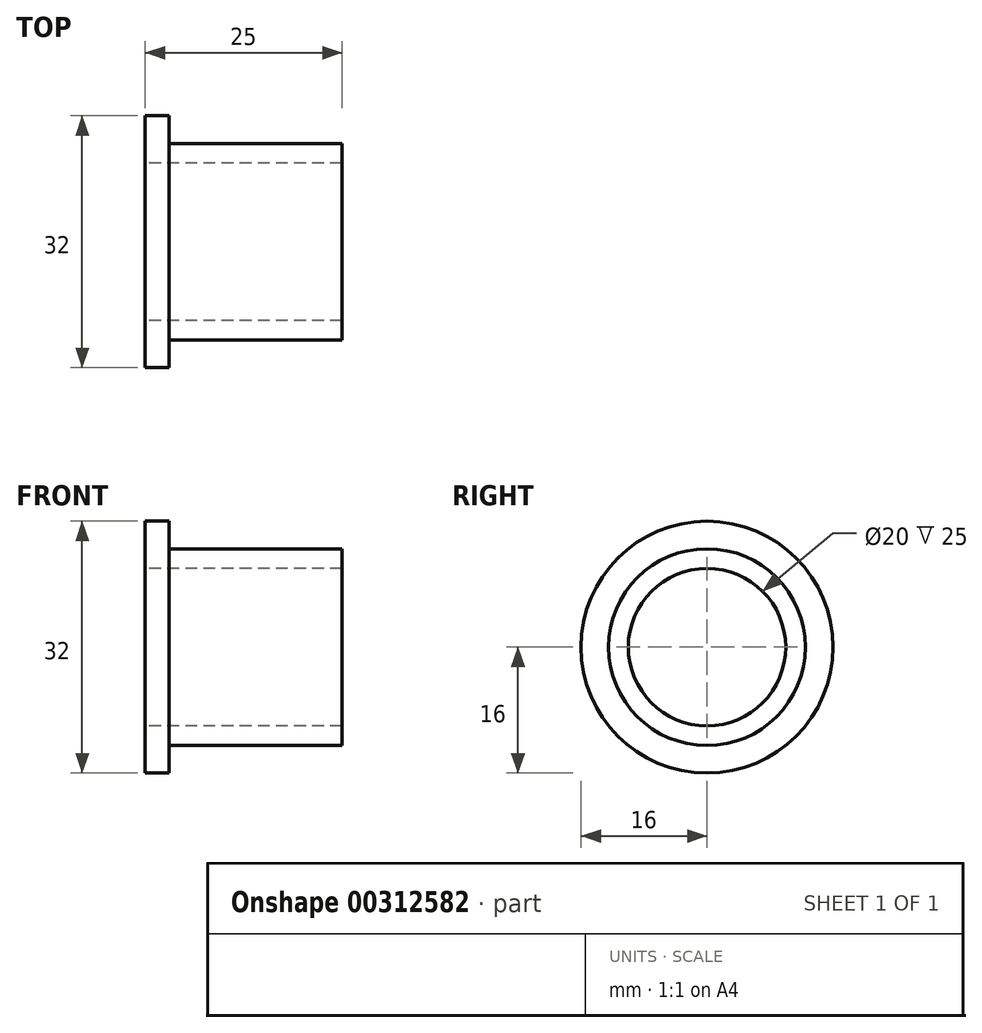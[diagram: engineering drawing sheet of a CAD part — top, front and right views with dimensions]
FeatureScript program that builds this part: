
annotation { "Feature Type Name" : "Feature", "Feature Type Description" : "" }
export const myFeature = defineFeature(function(context is Context, id is Id, definition is map)
    precondition{}
    {
        {
            var Q0;
            Q0=qCreatedBy(makeId("Front.planeOp"),FACE);
            var sketch = newSketch(context, id + "F0", { "sketchPlane" : qUnion([Q0])});
            skLineSegment(sketch, "E0", {"start": v(0, 16) * mm, "end": v(0, 10) * mm});
            skLineSegment(sketch, "E1", {"start": v(0, 10) * mm, "end": v(25, 10) * mm});
            skLineSegment(sketch, "E2", {"start": v(25, 10) * mm, "end": v(25, 12.5) * mm});
            skLineSegment(sketch, "E3", {"start": v(25, 12.5) * mm, "end": v(3, 12.5) * mm});
            skLineSegment(sketch, "E4", {"start": v(3, 12.5) * mm, "end": v(3, 16) * mm});
            skLineSegment(sketch, "E5", {"start": v(3, 16) * mm, "end": v(0, 16) * mm});
            skLineSegment(sketch, "E6", {"start": v(0, 0) * mm, "end": v(47.47, 0) * mm, "construction": true});
            skSolve(sketch);
        }
        {
            var Q0;
            Q0=makeQuery(id+"F0.imprint","IMPRINT",FACE,{"disambiguationData":[TD([[makeQuery(id+"F0.imprint","IMPRINT",EDGE,{"derivedFrom":sQuery(id+"F0.wireOp",EDGE,"E0")}),1.0]])]});
            var Q1;
            Q1=sQuery(id+"F0.wireOp",EDGE,"E6");
            revolve(context, id + "F1", {"entities" : qUnion([Q0]), "axis" : qUnion([Q1]), "revolveType" : RevolveType.FULL});
        }
    });
